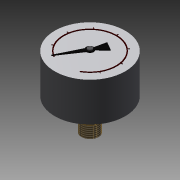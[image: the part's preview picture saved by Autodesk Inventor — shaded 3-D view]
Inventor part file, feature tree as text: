
AUTODESK INVENTOR PART (.ipt)
format: ipt  version: 2018 (Build 220112000, 112)  size: 171,520 bytes
history: native  units: mm
features: imported_body x1, thread x1
ambient origin geometry x8: Origin, YZ Plane, XZ Plane, XY Plane, X Axis, Y Axis, Z Axis, Center Point
bodies: Solid1 (feature_tree)
feature tree (2):
  imported_body  "Base1"
  thread  "Thread1"  [1 undecoded]
note: 1 required parameter value undecoded (feature->parameter linkage not recoverable at this tier; creation-order binding heuristic only, values carry confidence <= 0.55)
